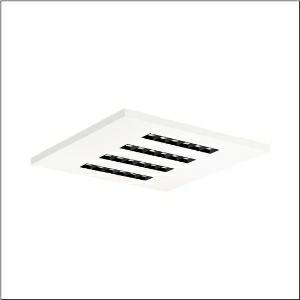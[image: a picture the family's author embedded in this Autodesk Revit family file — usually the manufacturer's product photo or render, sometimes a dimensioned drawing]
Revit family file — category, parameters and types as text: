
# Revit family: silica_r__21_square_51mx6kdu34w_c3bf
name_source: partatom
category: Lighting Fixtures
units: mm (PartAtom-declared; Revit-internal decimal feet)

## family parameters
Cut with Voids When Loaded = No
Host = Face
Light Source = No
Part Type = Normal
Room Calculation Point = No
Round Connector Dimension = Use Diameter
Shared = No

## types (1)
- --- (1 x LED, 4600 lm, 31.9 W, 3000K)
    Apparent Load = 32 VA
    CIE Flux Codes = 86 100 100 100 100
    Color Rendering = 80
    Color Temperature = 3000K
    Default Elevation = 1800 mm
    Description = Silica® 21 Square, office luminaire, primary light control with lens, of PMMA, primary anti-glare with reflector, of PC, black, CAT 2 (L<= 3000cd/m²), light emission: direct distribution, primary light characteristic: symmetric, installation type: lay-in mounting, LED, rated luminous flux: 4.600lm, luminous efficacy: 144lm/W, light colour: 830, colour temperature: 3000K, control gear: DALI 2, with terminal, 5-pole, mains connection: 220..240V, AC, 50/60Hz, rated input power: 31.9W, luminaire housing, of sheet steel, coated, traffic white (RAL 9016), module: M625, length: 622mm, width: 622mm, height: 33mm, protection rating (complete): IP20, insulation class (complete): insulation class I (protective earthing), certification: CE, ENEC, VDE, permissible operating ambient temperature: -20..+40°C, standard: EN 50419, packaging unit: 1 piece
    Height = 0 mm  [stored 0 ft]
    Lamp = 1 x LED
    Lamp Light Flux = 4600 lm
    Lamp Power = 31.9 W
    Lamp count = 1
    Length = 622 mm
    Luminous efficacy = 144 lm/W
    Manufacturer = Siteco
    ModVariant = No
    Model = 51MX6KDU34W
    Mounting Place = Ceiling
    Mounting Type = Recessed
    Number of Poles = 1
    OnlyDefault = Yes
    Power Factor = 1
    Product Name = Silica® 21 Square
    Product group = office luminaire | ceiling recessed
    ProductGroupID = 401
    Protection Class = Protection class I
    Protection Degree = IP 20
    RLX_Detail_Level = 1
    RLX_Emergency_Light_Flux = 0 lm
    RLX_Emergency_Type = 0
    RLX_Emergency_Type_DB = No
    RlxData = <blob elided: 21097 chars, md5=4a2c0226>
    Socket = socket
    Standby Power = 0 W
    System Light Flux = 4600 lm
    System Power = 32 W
    Type Comments = factory setting: luminous flux: 100 % | dim-lin: 254 | 430 mA
    Type Image = l_1275207.jpg
    URL = http://relux.com
    VarID = @adj_083992
    Voltage = 0 V
    Weight = 0.00 kg
    Width = 622 mm

note: [stored X ft] marks values corroborated as IEEE doubles in the binary element streams (Revit-internal decimal feet)

## geometry (parser evidence)
native form markers: Blend x4, Sweep x12
no freeform markers — native parametric forms only
